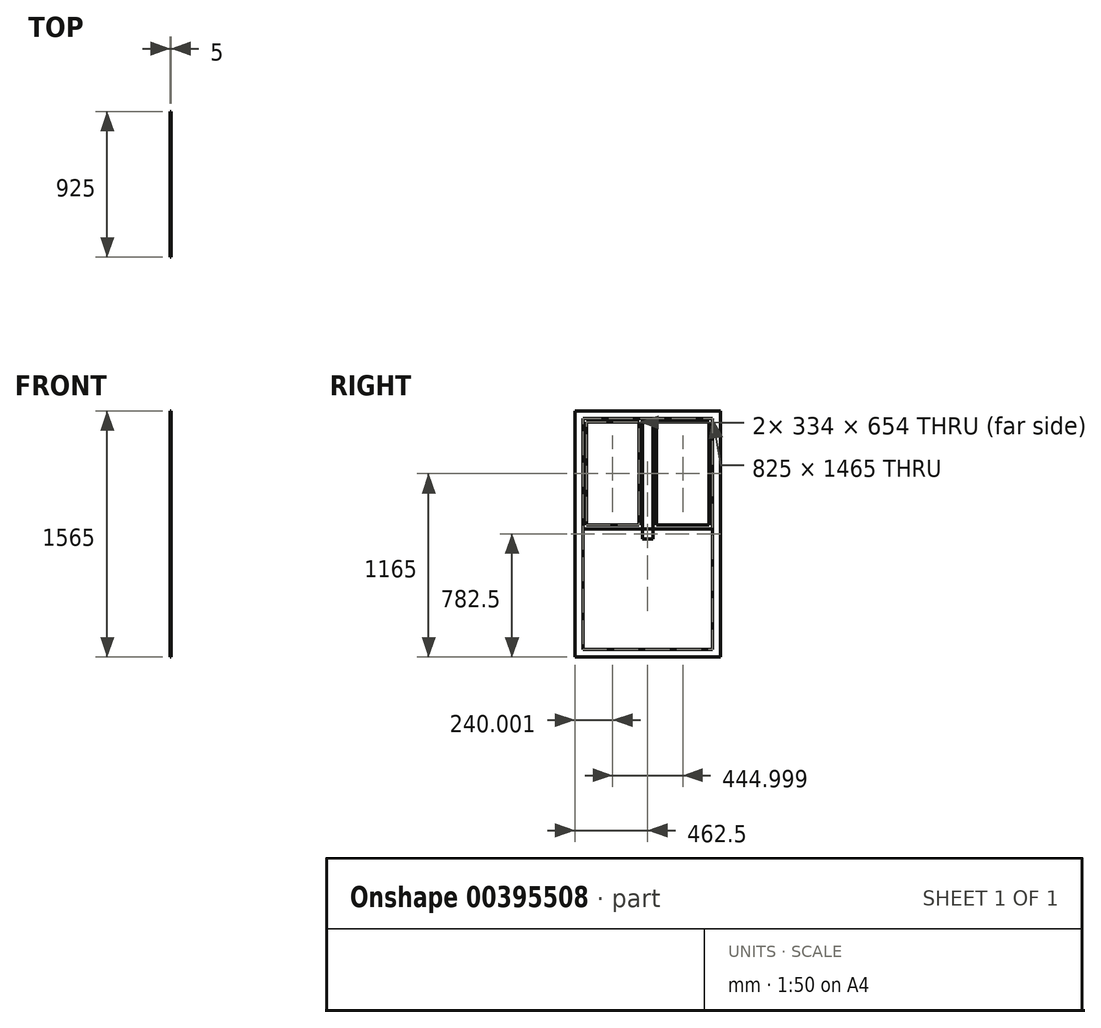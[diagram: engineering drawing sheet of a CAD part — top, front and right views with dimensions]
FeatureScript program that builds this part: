
annotation { "Feature Type Name" : "Feature", "Feature Type Description" : "" }
export const myFeature = defineFeature(function(context is Context, id is Id, definition is map)
    precondition{}
    {
        {
            var Q0;
            Q0=qCreatedBy(makeId("Right.planeOp"),FACE);
            var sketch = newSketch(context, id + "F0", { "sketchPlane" : qUnion([Q0])});
            skLineSegment(sketch, "E0.bottom", {"start": v(462.5, -782.5) * mm, "end": v(-462.5, -782.5) * mm});
            skLineSegment(sketch, "E0.top", {"start": v(462.5, 782.5) * mm, "end": v(-462.5, 782.5) * mm});
            skLineSegment(sketch, "E0.left", {"start": v(462.5, -782.5) * mm, "end": v(462.5, 782.5) * mm});
            skLineSegment(sketch, "E0.right", {"start": v(-462.5, -782.5) * mm, "end": v(-462.5, 782.5) * mm});
            skPoint(sketch, "E0.middle", {"position": v(0, 0) * mm});
            skLineSegment(sketch, "E1.bottom", {"start": v(412.5, -732.5) * mm, "end": v(-412.5, -732.5) * mm});
            skLineSegment(sketch, "E1.top", {"start": v(412.5, 732.5) * mm, "end": v(-412.5, 732.5) * mm});
            skLineSegment(sketch, "E1.left", {"start": v(412.5, -732.5) * mm, "end": v(412.5, 732.5) * mm});
            skLineSegment(sketch, "E1.right", {"start": v(-412.5, -732.5) * mm, "end": v(-412.5, 732.5) * mm});
            skLineSegment(sketch, "E2.bottom", {"start": v(412.5, -32.5) * mm, "end": v(-412.5, -32.5) * mm});
            skLineSegment(sketch, "E2.top", {"start": v(412.5, 32.5) * mm, "end": v(-412.5, 32.5) * mm});
            skLineSegment(sketch, "E2.left", {"start": v(412.5, -32.5) * mm, "end": v(412.5, 32.5) * mm});
            skLineSegment(sketch, "E2.right", {"start": v(-412.5, -32.5) * mm, "end": v(-412.5, 32.5) * mm});
            skLineSegment(sketch, "E3.bottom", {"start": v(32.5, -732.5) * mm, "end": v(-32.5, -732.5) * mm});
            skLineSegment(sketch, "E3.top", {"start": v(32.5, 732.5) * mm, "end": v(-32.5, 732.5) * mm});
            skLineSegment(sketch, "E3.left", {"start": v(32.5, -732.5) * mm, "end": v(32.5, 732.5) * mm});
            skLineSegment(sketch, "E3.right", {"start": v(-32.5, -732.5) * mm, "end": v(-32.5, 732.5) * mm});
            skSolve(sketch);
        }
        {
            var Q0;
            {var subQ0=sQuery(id+"F0.wireOp",EDGE,"E2.right");Q0=makeQuery(id+"F0.imprint","IMPRINT",FACE,{"disambiguationData":[TD([[makeQuery(id+"F0.imprint","IMPRINT",EDGE,{"derivedFrom":subQ0}),-1.0]])]});}
            var Q1;
            Q1=makeQuery(id+"F0.imprint","IMPRINT",FACE,{"disambiguationData":[TD([[makeQuery(id+"F0.imprint","IMPRINT",EDGE,{"derivedFrom":sQuery(id+"F0.wireOp",EDGE,"E0.bottom")}),-1.0]])]});
            var Q2;
            {var subQ5=sQuery(id+"F0.wireOp",EDGE,"E3.bottom");Q2=makeQuery(id+"F0.imprint","IMPRINT",FACE,{"disambiguationData":[TD([[makeQuery(id+"F0.imprint","IMPRINT",EDGE,{"derivedFrom":subQ5}),-1.0]])]});}
            var Q3;
            {var subQ0=sQuery(id+"F0.wireOp",EDGE,"E3.left");var subQ1=sQuery(id+"F0.wireOp",EDGE,"E2.bottom");var subQ2=makeQuery(id+"F0.imprint","INTERSECT",VERTEX,{"derivedFrom":[subQ1,subQ0]});Q3=makeQuery(id+"F0.imprint","IMPRINT",FACE,{"disambiguationData":[TD([[makeQuery(id+"F0.imprint","IMPRINT",EDGE,{"disambiguationData":[TD([[subQ2,-1.0]])],"derivedFrom":subQ1}),-1.0]])]});}
            var Q4;
            {var subQ0=sQuery(id+"F0.wireOp",EDGE,"E2.left");Q4=makeQuery(id+"F0.imprint","IMPRINT",FACE,{"disambiguationData":[TD([[makeQuery(id+"F0.imprint","IMPRINT",EDGE,{"derivedFrom":subQ0}),1.0]])]});}
            var Q5;
            {var subQ5=sQuery(id+"F0.wireOp",EDGE,"E3.top");Q5=makeQuery(id+"F0.imprint","IMPRINT",FACE,{"disambiguationData":[TD([[makeQuery(id+"F0.imprint","IMPRINT",EDGE,{"derivedFrom":subQ5}),1.0]])]});}
            extrude(context, id + "F1", {"entities" : qUnion([Q0, Q1, Q2, Q3, Q4, Q5]), "depth" : 5 * mm});
        }
        {
            var Q0;
            Q0=qCreatedBy(makeId("Right.planeOp"),FACE);
            cPlane(context, id + "F2", {"entities" : qUnion([Q0]), "cplaneType" : CPlaneType.OFFSET, "offset" : 0.8 * mm, "width" : 150 * mm, "height" : 150 * mm});
        }
        {
            var Q0;
            Q0=qCreatedBy(id+"F2.planeOp",FACE);
            var sketch = newSketch(context, id + "F3", { "sketchPlane" : qUnion([Q0])});
            skLineSegment(sketch, "E4.0", {"start": v(412.5, 32.5) * mm, "end": v(412.5, 732.5) * mm});
            skLineSegment(sketch, "E5.0", {"start": v(412.5, 732.5) * mm, "end": v(32.5, 732.5) * mm});
            skLineSegment(sketch, "E6.0", {"start": v(32.5, 32.5) * mm, "end": v(32.5, 732.5) * mm});
            skLineSegment(sketch, "E7.0", {"start": v(412.5, 32.5) * mm, "end": v(32.5, 32.5) * mm});
            skLineSegment(sketch, "E8.0", {"start": v(389.5, 709.5) * mm, "end": v(55.5, 709.5) * mm});
            skLineSegment(sketch, "E8.1", {"start": v(389.5, 55.5) * mm, "end": v(389.5, 709.5) * mm});
            skLineSegment(sketch, "E8.2", {"start": v(389.5, 55.5) * mm, "end": v(55.5, 55.5) * mm});
            skLineSegment(sketch, "E8.3", {"start": v(55.5, 55.5) * mm, "end": v(55.5, 709.5) * mm});
            skLineSegment(sketch, "E9.MirrorCS", {"start": v(-55.5, 55.5) * mm, "end": v(-55.5, 709.5) * mm});
            skLineSegment(sketch, "E10.MirrorCS", {"start": v(-32.5, 32.5) * mm, "end": v(-32.5, 732.5) * mm});
            skLineSegment(sketch, "E11.MirrorCS", {"start": v(-412.5, 732.5) * mm, "end": v(-32.5, 732.5) * mm});
            skLineSegment(sketch, "E12.MirrorCS", {"start": v(-412.5, 32.5) * mm, "end": v(-412.5, 732.5) * mm});
            skLineSegment(sketch, "E13.MirrorCS", {"start": v(-412.5, 32.5) * mm, "end": v(-32.5, 32.5) * mm});
            skLineSegment(sketch, "E14.MirrorCS", {"start": v(-389.5, 55.5) * mm, "end": v(-55.5, 55.5) * mm});
            skLineSegment(sketch, "E15.MirrorCS", {"start": v(-389.5, 55.5) * mm, "end": v(-389.5, 709.5) * mm});
            skLineSegment(sketch, "E16.MirrorCS", {"start": v(-389.5, 709.5) * mm, "end": v(-55.5, 709.5) * mm});
            skSolve(sketch);
        }
        {
            var Q0;
            Q0=qSketchRegion(id+"F3",true);
            extrude(context, id + "F4", {"entities" : qUnion([Q0]), "operationType" : NewBodyOperationType.ADD, "depth" : 0.25 * mm});
        }
    });
